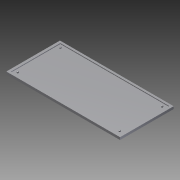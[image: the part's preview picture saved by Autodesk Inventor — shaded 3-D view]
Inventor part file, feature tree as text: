
AUTODESK INVENTOR PART (.ipt)
format: ipt  version: 2012 SP2 (Build 160219200, 219)  size: 105,984 bytes
history: native  units: in
note: dims shown in document units (in); Inventor stores cm internally (conversion verified against a paired STEP export)
features: extrude x3, sketch x3, reference x3, fillet x1
ambient origin geometry x8: Origin, YZ Plane, XZ Plane, XY Plane, X Axis, Y Axis, Z Axis, Center Point
bodies: Solid1 (feature_tree)
feature tree (10):
  extrude  "Extrusion1"  Depth=0.5in
  extrude  "Extrusion2"  Depth=0.1875in TaperAngle=0.0deg
  extrude  "Extrusion3"  Depth=0.4088in
  fillet  "Fillet1"  Radius=0.3in
  sketch  "Sketch1"  dims[d0=13.0in d1=0.0in d2=0.5in]
  reference  "Reference1"
  reference  "Reference2"
  sketch  "Sketch2"  dims[d3=0.5in d4=0.1875in d5=0.0in]
  reference  "Reference3"
  sketch  "Sketch3"  dims[d6=0.855in d7=0.4088in d8=0.3in d9=0.0in d10=0.125in]
